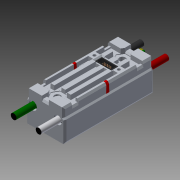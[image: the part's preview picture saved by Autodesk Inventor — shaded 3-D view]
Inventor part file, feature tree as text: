
AUTODESK INVENTOR PART (.ipt)
format: ipt  version: 2016 SP1 (Build 200210100, 210)  size: 3,524,096 bytes
history: native  units: in
note: dims shown in document units (in); Inventor stores cm internally (conversion verified against a paired STEP export)
features: plane x2, split x2, boolean_combine x1, imported_body x1
ambient origin geometry x8: Origin, YZ Plane, XZ Plane, XY Plane, X Axis, Y Axis, Z Axis, Center Point
bodies: Body1 (feature_tree)
feature tree (6):
  boolean_combine  "Combine11"
  plane  "Work Plane1"
  split  "Split1"
  plane  "Work Plane2"
  split  "Split2"
  imported_body  "Base1"
